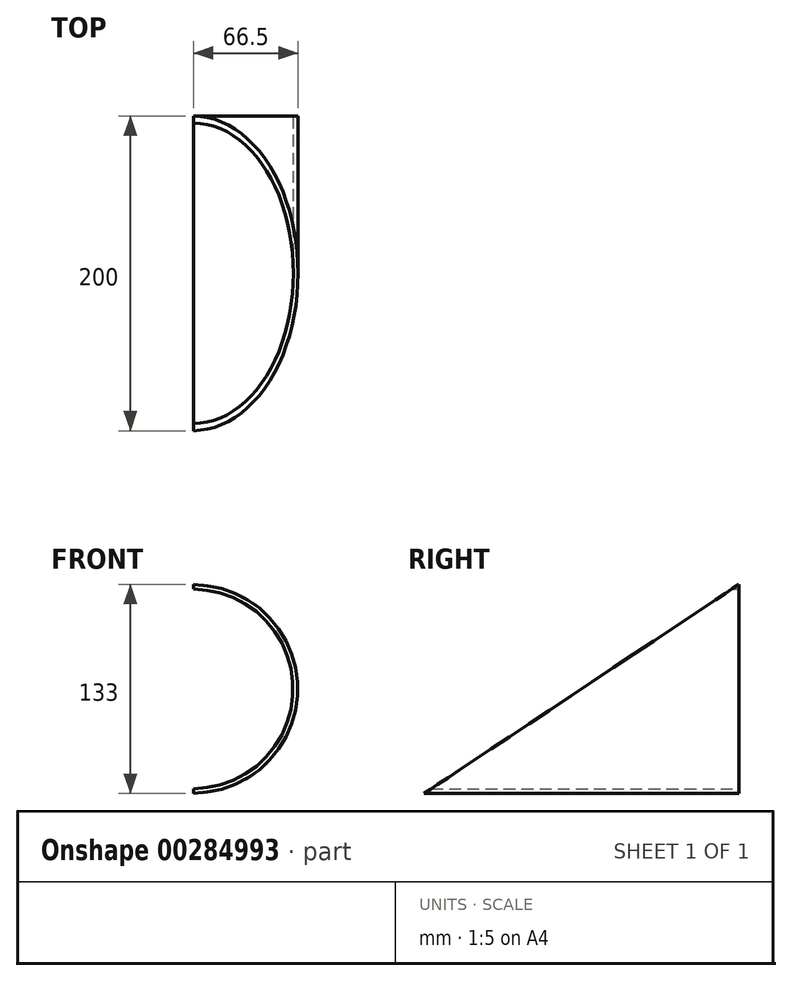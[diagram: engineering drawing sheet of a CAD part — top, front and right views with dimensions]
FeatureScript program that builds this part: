
annotation { "Feature Type Name" : "Feature", "Feature Type Description" : "" }
export const myFeature = defineFeature(function(context is Context, id is Id, definition is map)
    precondition{}
    {
        {
            var Q0;
            Q0=qCreatedBy(makeId("Front.planeOp"),FACE);
            var sketch = newSketch(context, id + "F0", { "sketchPlane" : qUnion([Q0])});
            skArc(sketch, "E0", {"start": v(0, -63.5) * mm, "mid": v(63.5, 0) * mm, "end": v(0, 63.5) * mm});
            skArc(sketch, "E1.0", {"start": v(0, -66.5) * mm, "mid": v(66.5, 0) * mm, "end": v(0, 66.5) * mm});
            skLineSegment(sketch, "E2", {"start": v(0, -66.5) * mm, "end": v(0, -63.5) * mm});
            skLineSegment(sketch, "E3.trimOffspring", {"start": v(0, 63.5) * mm, "end": v(0, 66.5) * mm});
            skSolve(sketch);
        }
        {
            var Q0;
            Q0=makeQuery(id+"F0.imprint","IMPRINT",FACE,{"disambiguationData":[TD([[makeQuery(id+"F0.imprint","IMPRINT",EDGE,{"derivedFrom":sQuery(id+"F0.wireOp",EDGE,"E0")}),-1.0]])]});
            extrude(context, id + "F1", {"entities" : qUnion([Q0]), "endBound" : BoundingType.SYMMETRIC, "depth" : 200 * mm});
        }
        {
            var Q0;
            Q0=qCreatedBy(makeId("Right.planeOp"),FACE);
            var sketch = newSketch(context, id + "F2", { "sketchPlane" : qUnion([Q0])});
            skPoint(sketch, "E4.0", {"position": v(-100, -66.5) * mm});
            skPoint(sketch, "E5.0", {"position": v(100, 66.5) * mm});
            skLineSegment(sketch, "E6", {"start": v(-100, -66.5) * mm, "end": v(100, 66.5) * mm});
            skLineSegment(sketch, "E7", {"start": v(100, 78.44) * mm, "end": v(-100, 78.44) * mm});
            skLineSegment(sketch, "E8", {"start": v(-100, 78.44) * mm, "end": v(-100, -66.5) * mm});
            skLineSegment(sketch, "E9", {"start": v(100, 66.5) * mm, "end": v(100, 78.44) * mm});
            skSolve(sketch);
        }
        {
            var Q0;
            Q0=makeQuery(id+"F2.imprint","IMPRINT",FACE,{"disambiguationData":[TD([[makeQuery(id+"F2.imprint","IMPRINT",EDGE,{"derivedFrom":sQuery(id+"F2.wireOp",EDGE,"E6")}),1.0]])]});
            extrude(context, id + "F3", {"entities" : qUnion([Q0]), "operationType" : NewBodyOperationType.REMOVE, "endBound" : BoundingType.THROUGH_ALL, "depth" : 25 * mm});
        }
    });
